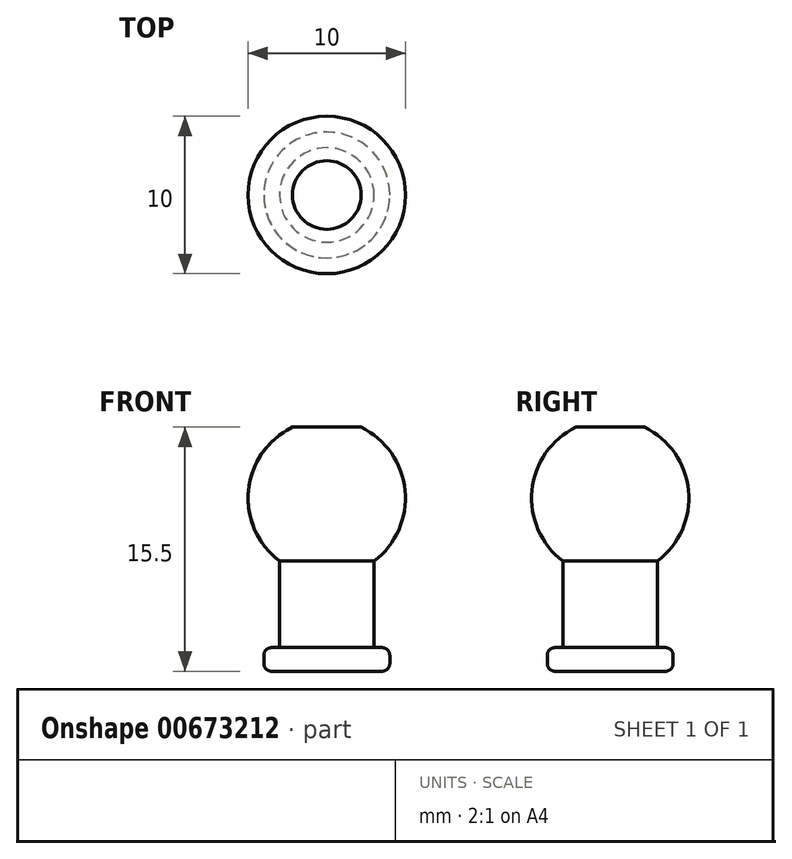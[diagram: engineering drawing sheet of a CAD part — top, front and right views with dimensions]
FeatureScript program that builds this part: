
annotation { "Feature Type Name" : "Feature", "Feature Type Description" : "" }
export const myFeature = defineFeature(function(context is Context, id is Id, definition is map)
    precondition{}
    {
        {
            var Q0;
            Q0=qCreatedBy(makeId("Right.planeOp"),FACE);
            var sketch = newSketch(context, id + "F0", { "sketchPlane" : qUnion([Q0])});
            skArc(sketch, "E0", {"start": v(-2.18, 4.5) * mm, "mid": v(-4.98, 0.48) * mm, "end": v(-3, -4) * mm});
            skLineSegment(sketch, "E1", {"start": v(0, 4.5) * mm, "end": v(0, -5) * mm, "construction": true});
            skLineSegment(sketch, "E2", {"start": v(-3, -5) * mm, "end": v(-3, -4) * mm});
            skLineSegment(sketch, "E3", {"start": v(-3, -5) * mm, "end": v(-3, -9.5) * mm});
            skLineSegment(sketch, "E4", {"start": v(-3, -9.5) * mm, "end": v(-4, -9.5) * mm});
            skLineSegment(sketch, "E5", {"start": v(-4, -9.5) * mm, "end": v(-4, -11) * mm});
            skLineSegment(sketch, "E6", {"start": v(-4, -11) * mm, "end": v(0, -11) * mm});
            skLineSegment(sketch, "E7", {"start": v(0, -11) * mm, "end": v(0, 4.5) * mm});
            skLineSegment(sketch, "E8", {"start": v(0, 4.5) * mm, "end": v(-2.18, 4.5) * mm});
            skPoint(sketch, "E9.orphan", {"position": v(0, 5) * mm});
            skSolve(sketch);
        }
        {
            var Q0;
            Q0=qSketchRegion(id+"F0",true);
            var Q1;
            Q1=sQuery(id+"F0.wireOp",EDGE,"E7");
            revolve(context, id + "F1", {"entities" : qUnion([Q0]), "axis" : qUnion([Q1]), "revolveType" : RevolveType.FULL});
        }
        {
            var Q0;
            Q0=makeQuery(id+"F1.opRevolve","SWEPT_FACE",FACE,{"disambiguationData":[OSD([sQuery(id+"F0.wireOp",EDGE,"E5")])]});
            fillet(context, id + "F2", {"entities" : qUnion([Q0]), "radius" : .5 * mm, "tangentPropagation" : true, "allowEdgeOverflow" : false});
        }
    });
